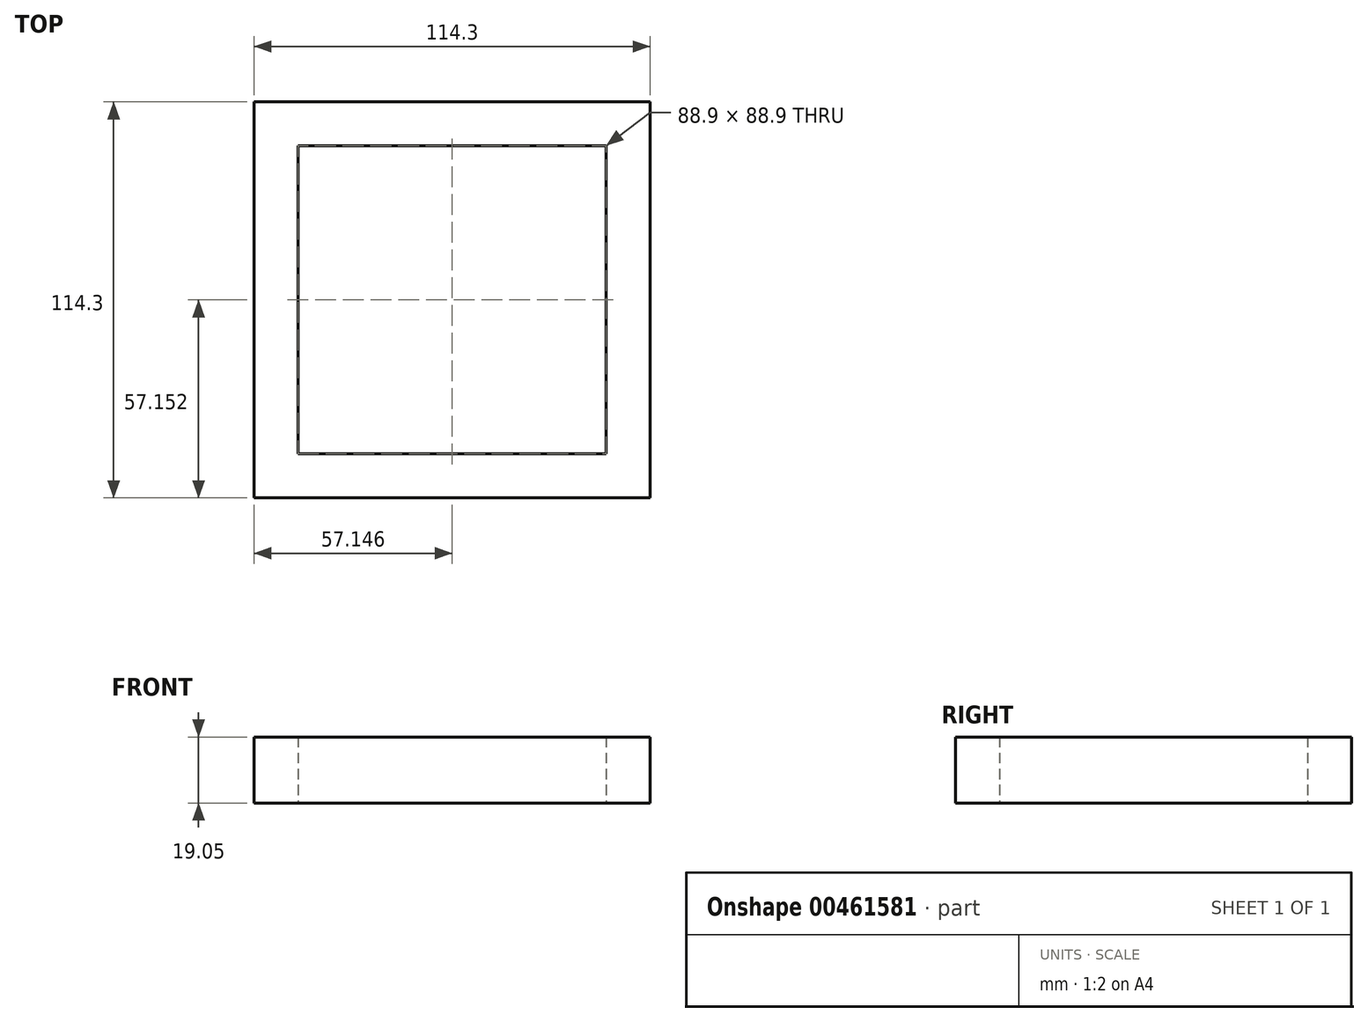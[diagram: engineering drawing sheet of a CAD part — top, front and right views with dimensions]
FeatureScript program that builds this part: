
annotation { "Feature Type Name" : "Feature", "Feature Type Description" : "" }
export const myFeature = defineFeature(function(context is Context, id is Id, definition is map)
    precondition{}
    {
        {
            var Q0;
            Q0=qCreatedBy(makeId("Top.planeOp"),FACE);
            var sketch = newSketch(context, id + "F0", { "sketchPlane" : qUnion([Q0])});
            skLineSegment(sketch, "E0.bottom", {"start": v(-49.1, -57.58) * mm, "end": v(65.2, -57.58) * mm});
            skLineSegment(sketch, "E0.top", {"start": v(-49.1, 56.72) * mm, "end": v(65.2, 56.72) * mm});
            skLineSegment(sketch, "E0.left", {"start": v(-49.1, -57.58) * mm, "end": v(-49.1, 56.72) * mm});
            skLineSegment(sketch, "E0.right", {"start": v(65.2, -57.58) * mm, "end": v(65.2, 56.72) * mm});
            skLineSegment(sketch, "E1.bottom", {"start": v(-36.4, -44.88) * mm, "end": v(52.5, -44.88) * mm});
            skLineSegment(sketch, "E1.top", {"start": v(-36.4, 44.02) * mm, "end": v(52.5, 44.02) * mm});
            skLineSegment(sketch, "E1.left", {"start": v(-36.4, -44.88) * mm, "end": v(-36.4, 44.02) * mm});
            skLineSegment(sketch, "E1.right", {"start": v(52.5, -44.88) * mm, "end": v(52.5, 44.02) * mm});
            skSolve(sketch);
        }
        {
            var Q0;
            Q0=makeQuery(id+"F0.imprint","IMPRINT",FACE,{"disambiguationData":[TD([[makeQuery(id+"F0.imprint","IMPRINT",EDGE,{"derivedFrom":sQuery(id+"F0.wireOp",EDGE,"E0.bottom")}),1.0]])]});
            extrude(context, id + "F1", {"entities" : qUnion([Q0]), "depth" : 19.05 * mm});
        }
    });
